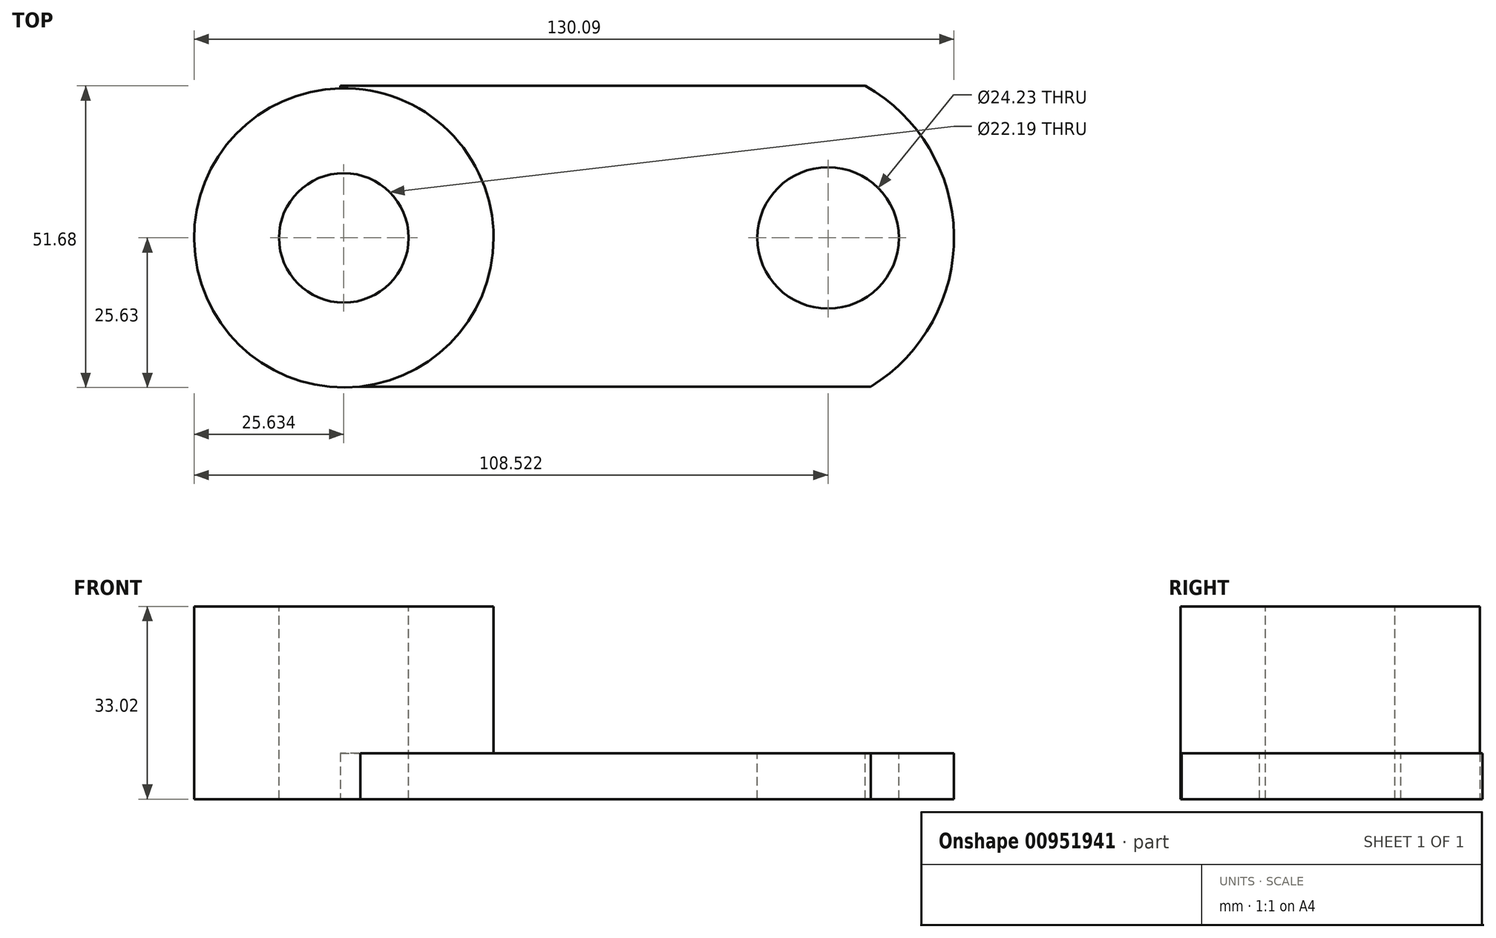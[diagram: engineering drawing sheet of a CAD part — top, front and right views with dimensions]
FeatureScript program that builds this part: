
annotation { "Feature Type Name" : "Feature", "Feature Type Description" : "" }
export const myFeature = defineFeature(function(context is Context, id is Id, definition is map)
    precondition{}
    {
        {
            var Q0;
            Q0=qCreatedBy(makeId("Top.planeOp"),FACE);
            var sketch = newSketch(context, id + "F0", { "sketchPlane" : qUnion([Q0])});
            skCircle(sketch, "E0", {"center": v(-47.06, 0) * mm, "radius": 25.63 * mm});
            skLineSegment(sketch, "E1.bottom", {"start": v(-47.06, 25.63) * mm, "end": v(60, 25.63) * mm});
            skLineSegment(sketch, "E1.top", {"start": v(-47.06, -25.76) * mm, "end": v(60, -25.76) * mm});
            skLineSegment(sketch, "E1.left", {"start": v(-47.06, -25.63) * mm, "end": v(-47.06, -25.76) * mm});
            skLineSegment(sketch, "E1.right", {"start": v(60, 25.63) * mm, "end": v(60, -25.76) * mm});
            skSolve(sketch);
        }
        {
            var Q0;
            {var subQ0=sQuery(id+"F0.wireOp",EDGE,"E0");var subQ1=makeQuery(id+"F0.imprint","INTERSECT",VERTEX,{"derivedFrom":[subQ0,sQuery(id+"F0.wireOp",EDGE,"E1.bottom")]});Q0=makeQuery(id+"F0.imprint","IMPRINT",FACE,{"disambiguationData":[TD([[makeQuery(id+"F0.imprint","IMPRINT",EDGE,{"disambiguationData":[TD([[subQ1,-1.0]])],"derivedFrom":subQ0}),1.0]])]});}
            extrude(context, id + "F1", {"entities" : qUnion([Q0]), "depth" : 33.02 * mm, "offsetDistance" : 25.4 * mm});
        }
        {
            var Q0;
            Q0=qCreatedBy(makeId("Top.planeOp"),FACE);
            var sketch = newSketch(context, id + "F2", { "sketchPlane" : qUnion([Q0])});
            skLineSegment(sketch, "E2", {"start": v(-47.63, 26.05) * mm, "end": v(59.72, 26.05) * mm});
            skLineSegment(sketch, "E3", {"start": v(-47.63, 26.05) * mm, "end": v(-47.63, -25.47) * mm});
            skLineSegment(sketch, "E4", {"start": v(-47.63, -25.47) * mm, "end": v(59.72, -25.47) * mm});
            skLineSegment(sketch, "E5", {"start": v(59.72, 26.05) * mm, "end": v(59.72, -25.47) * mm});
            skSolve(sketch);
        }
        {
            var Q0;
            Q0=makeQuery(id+"F2.imprint","IMPRINT",FACE,{"disambiguationData":[TD([[makeQuery(id+"F2.imprint","IMPRINT",EDGE,{"derivedFrom":sQuery(id+"F2.wireOp",EDGE,"E2")}),-1.0]])]});
            extrude(context, id + "F3", {"entities" : qUnion([Q0]), "operationType" : NewBodyOperationType.ADD, "depth" : 7.87 * mm, "offsetDistance" : 25.4 * mm});
        }
        {
            var Q0;
            Q0=makeQuery(id+"F3.opExtrude","CAP_FACE",FACE,{"disambiguationData":[OSD([sQuery(id+"F2.wireOp",EDGE,"E2"),sQuery(id+"F2.wireOp",EDGE,"E3"),sQuery(id+"F2.wireOp",EDGE,"E4"),sQuery(id+"F2.wireOp",EDGE,"E5")])],"isStart":false});
            var sketch = newSketch(context, id + "F4", { "sketchPlane" : qUnion([Q0])});
            skCircle(sketch, "E6", {"center": v(35.83, 0) * mm, "radius": 12.11 * mm});
            skSolve(sketch);
        }
        {
            var Q0;
            Q0=makeQuery(id+"F1.opExtrude","CAP_FACE",FACE,{"disambiguationData":[OSD([sQuery(id+"F0.wireOp",EDGE,"E0")])],"isStart":false});
            var sketch = newSketch(context, id + "F5", { "sketchPlane" : qUnion([Q0])});
            skCircle(sketch, "E7", {"center": v(-47.06, 0) * mm, "radius": 11.1 * mm});
            skSolve(sketch);
        }
        {
            var Q0;
            Q0=makeQuery(id+"F5.imprint","IMPRINT",FACE,{"disambiguationData":[TD([[makeQuery(id+"F5.imprint","IMPRINT",EDGE,{"derivedFrom":sQuery(id+"F5.wireOp",EDGE,"E7")}),1.0]])]});
            var Q1;
            Q1=makeQuery(id+"F4.imprint","IMPRINT",FACE,{"disambiguationData":[TD([[makeQuery(id+"F4.imprint","IMPRINT",EDGE,{"derivedFrom":sQuery(id+"F4.wireOp",EDGE,"E6")}),1.0]])]});
            extrude(context, id + "F6", {"entities" : qUnion([Q0, Q1]), "operationType" : NewBodyOperationType.REMOVE, "oppositeDirection" : true, "depth" : 81.53 * mm, "offsetDistance" : 25.4 * mm});
        }
        {
            var Q0;
            Q0=makeQuery(id+"F3.opExtrude","CAP_FACE",FACE,{"disambiguationData":[OSD([sQuery(id+"F2.wireOp",EDGE,"E2"),sQuery(id+"F2.wireOp",EDGE,"E3"),sQuery(id+"F2.wireOp",EDGE,"E4"),sQuery(id+"F2.wireOp",EDGE,"E5")])],"isStart":false});
            var sketch = newSketch(context, id + "F7", { "sketchPlane" : qUnion([Q0])});
            skCircle(sketch, "E8", {"center": v(27.49, 0) * mm, "radius": 29.9 * mm});
            skSolve(sketch);
        }
        {
            var Q0;
            {var subQ5=makeQuery(id+"F3.opExtrude","CAP_EDGE",EDGE,{"disambiguationData":[OSD([sQuery(id+"F2.wireOp",EDGE,"E5")])],"isStart":false});Q0=makeQuery(id+"F7.imprint","IMPRINT",FACE,{"disambiguationData":[TD([[makeQuery(id+"F7.imprint","IMPRINT",EDGE,{"derivedFrom":subQ5}),-1.0]])]});}
            extrude(context, id + "F8", {"entities" : qUnion([Q0]), "operationType" : NewBodyOperationType.REMOVE, "oppositeDirection" : true, "depth" : 25.4 * mm, "offsetDistance" : 25.4 * mm});
        }
    });
